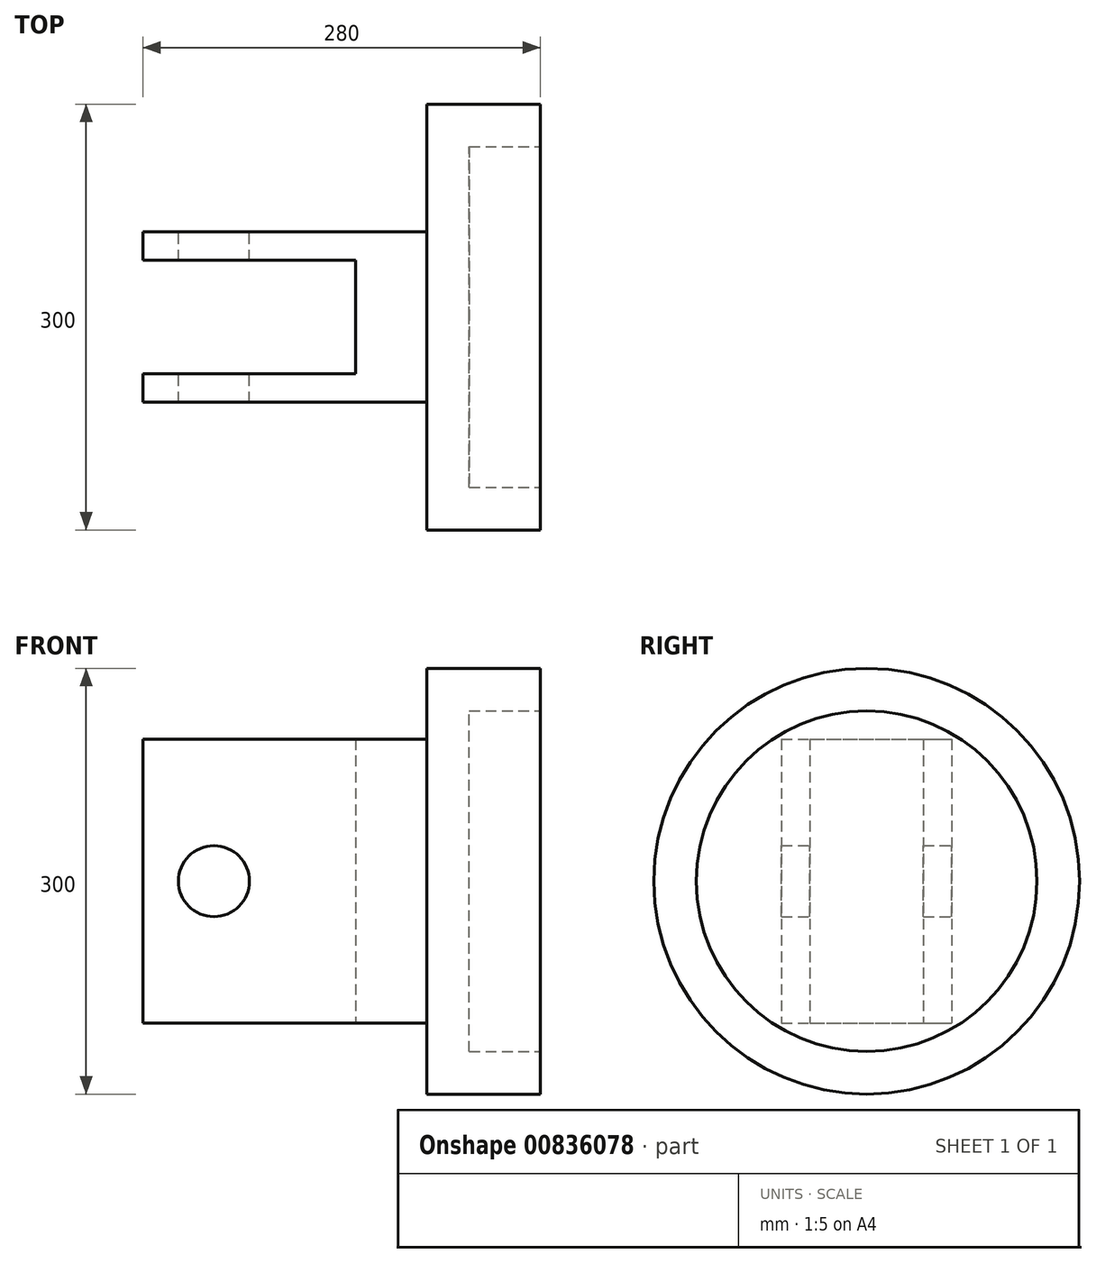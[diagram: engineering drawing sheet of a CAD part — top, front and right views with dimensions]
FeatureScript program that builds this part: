
annotation { "Feature Type Name" : "Feature", "Feature Type Description" : "" }
export const myFeature = defineFeature(function(context is Context, id is Id, definition is map)
    precondition{}
    {
        {
            var Q0;
            Q0=qCreatedBy(makeId("Front.planeOp"),FACE);
            var sketch = newSketch(context, id + "F0", { "sketchPlane" : qUnion([Q0])});
            skLineSegment(sketch, "E0.bottom", {"start": v(0, 100) * mm, "end": v(-200, 100) * mm});
            skLineSegment(sketch, "E0.top", {"start": v(0, -100) * mm, "end": v(-200, -100) * mm});
            skLineSegment(sketch, "E0.left", {"start": v(0, 100) * mm, "end": v(0, -100) * mm});
            skLineSegment(sketch, "E0.right", {"start": v(-200, 100) * mm, "end": v(-200, -100) * mm});
            skCircle(sketch, "E1", {"center": v(-150, 0) * mm, "radius": 25 * mm});
            skSolve(sketch);
        }
        {
            var Q0;
            Q0 = qSketchRegion(id + "F0", true);
            extrude(context, id + "F1", {"entities" : qUnion([Q0]), "endBound" : BoundingType.SYMMETRIC, "depth" : 120 * mm, "offsetDistance" : 25 * mm});
        }
        {
            var Q0;
            Q0=qCreatedBy(makeId("Front.planeOp"),FACE);
            var sketch = newSketch(context, id + "F2", { "sketchPlane" : qUnion([Q0])});
            skLineSegment(sketch, "E2.bottom", {"start": v(-200, 100) * mm, "end": v(-50, 100) * mm});
            skLineSegment(sketch, "E2.top", {"start": v(-200, -100) * mm, "end": v(-50, -100) * mm});
            skLineSegment(sketch, "E2.left", {"start": v(-200, 100) * mm, "end": v(-200, -100) * mm});
            skLineSegment(sketch, "E2.right", {"start": v(-50, 100) * mm, "end": v(-50, -100) * mm});
            skSolve(sketch);
        }
        {
            var Q0;
            Q0 = qSketchRegion(id + "F2", true);
            extrude(context, id + "F3", {"entities" : qUnion([Q0]), "operationType" : NewBodyOperationType.REMOVE, "endBound" : BoundingType.SYMMETRIC, "depth" : 80 * mm, "offsetDistance" : 25 * mm});
        }
        {
            var Q0;
            Q0=makeQuery(id+"F1.opExtrude","SWEPT_FACE",FACE,{"disambiguationData":[OSD([sQuery(id+"F0.wireOp",EDGE,"E0.left")])]});
            var sketch = newSketch(context, id + "F4", { "sketchPlane" : qUnion([Q0])});
            skCircle(sketch, "E3", {"center": v(0, 0) * mm, "radius": 150 * mm});
            skSolve(sketch);
        }
        {
            var Q0;
            Q0 = qSketchRegion(id + "F4", true);
            extrude(context, id + "F5", {"entities" : qUnion([Q0]), "operationType" : NewBodyOperationType.ADD, "depth" : 80 * mm, "offsetDistance" : 25 * mm});
        }
        {
            var Q0;
            Q0=makeQuery(id+"F5.opExtrude","CAP_FACE",FACE,{"disambiguationData":[OSD([sQuery(id+"F4.wireOp",EDGE,"E3")])],"isStart":false});
            var sketch = newSketch(context, id + "F6", { "sketchPlane" : qUnion([Q0])});
            skCircle(sketch, "E4", {"center": v(0, 0) * mm, "radius": 120 * mm});
            skSolve(sketch);
        }
        {
            var Q0;
            Q0 = qSketchRegion(id + "F6", true);
            extrude(context, id + "F7", {"entities" : qUnion([Q0]), "operationType" : NewBodyOperationType.REMOVE, "oppositeDirection" : true, "depth" : 50 * mm, "offsetDistance" : 25 * mm});
        }
    });
